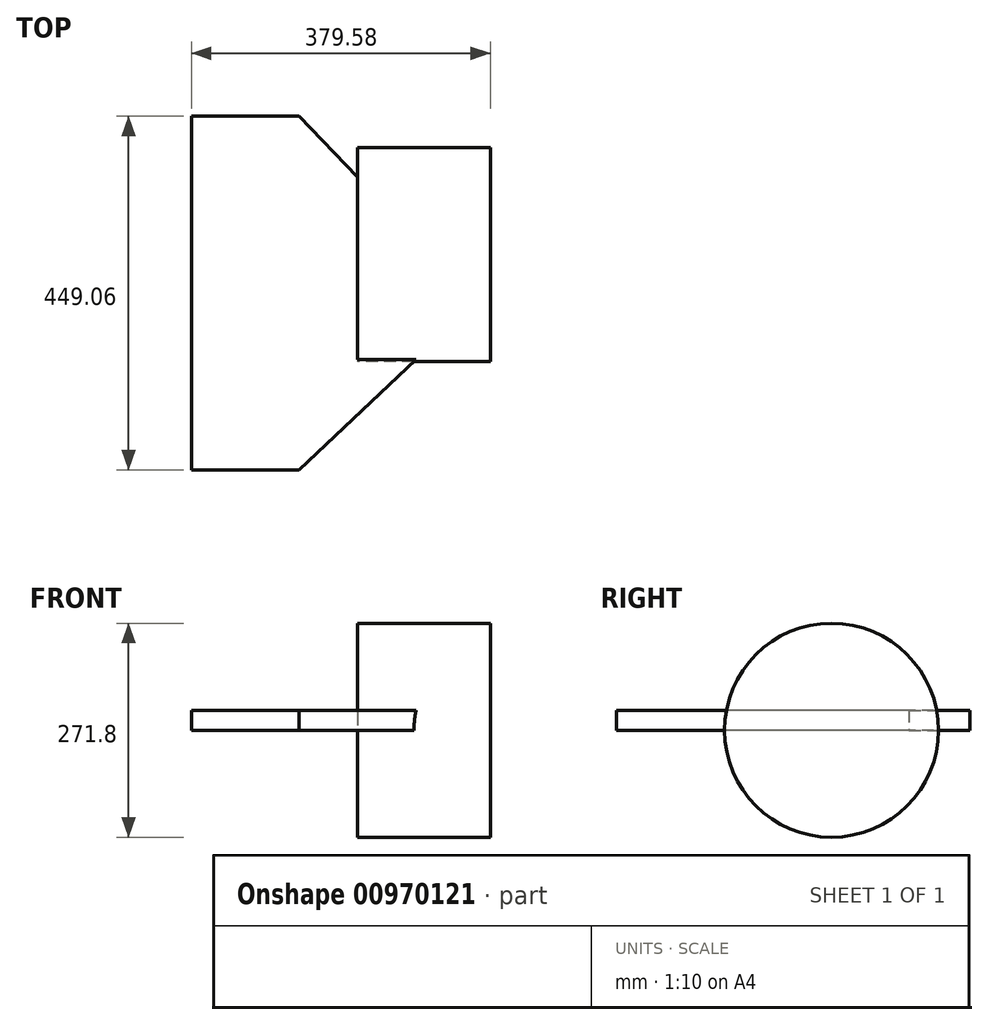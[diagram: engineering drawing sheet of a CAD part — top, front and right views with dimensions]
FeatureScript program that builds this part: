
annotation { "Feature Type Name" : "Feature", "Feature Type Description" : "" }
export const myFeature = defineFeature(function(context is Context, id is Id, definition is map)
    precondition{}
    {
        {
            var Q0;
            Q0=qCreatedBy(makeId("Top.planeOp"),FACE);
            var sketch = newSketch(context, id + "F0", { "sketchPlane" : qUnion([Q0])});
            skLineSegment(sketch, "E0.bottom", {"start": v(74.12, 196.1) * mm, "end": v(243.05, 196.1) * mm});
            skLineSegment(sketch, "E0.top", {"start": v(74.12, 60.2) * mm, "end": v(243.05, 60.2) * mm});
            skLineSegment(sketch, "E0.left", {"start": v(74.12, 196.1) * mm, "end": v(74.12, 60.2) * mm});
            skLineSegment(sketch, "E0.right", {"start": v(243.05, 196.1) * mm, "end": v(243.05, 60.2) * mm});
            skSolve(sketch);
        }
        {
            var Q0;
            Q0=qCreatedBy(makeId("Top.planeOp"),FACE);
            var sketch = newSketch(context, id + "F1", { "sketchPlane" : qUnion([Q0])});
            skLineSegment(sketch, "E1.bottom", {"start": v(-136.53, 235.94) * mm, "end": v(0, 235.94) * mm});
            skLineSegment(sketch, "E1.top", {"start": v(-136.53, -213.12) * mm, "end": v(0, -213.12) * mm});
            skLineSegment(sketch, "E1.left", {"start": v(-136.53, 235.94) * mm, "end": v(-136.53, -213.12) * mm});
            skLineSegment(sketch, "E2", {"start": v(0, -213.12) * mm, "end": v(226.4, 0) * mm});
            skLineSegment(sketch, "E3", {"start": v(226.4, 0) * mm, "end": v(0, 235.94) * mm});
            skSolve(sketch);
        }
        {
            var Q0;
            Q0=makeQuery(id+"F0.imprint","IMPRINT",FACE,{"disambiguationData":[TD([[makeQuery(id+"F0.imprint","IMPRINT",EDGE,{"derivedFrom":sQuery(id+"F0.wireOp",EDGE,"E0.bottom")}),-1.0]])]});
            var Q1;
            Q1=sQuery(id+"F0.wireOp",EDGE,"E0.top");
            revolve(context, id + "F2", {"surfaceOperationType" : NewSurfaceOperationType.NEW, "entities" : qUnion([Q0]), "axis" : qUnion([Q1]), "revolveType" : RevolveType.FULL});
        }
        {
            var Q0;
            Q0 = qSketchRegion(id + "F1", true);
            extrude(context, id + "F3", {"entities" : qUnion([Q0]), "operationType" : NewBodyOperationType.ADD, "depth" : 25 * mm, "offsetDistance" : 25 * mm});
        }
    });
